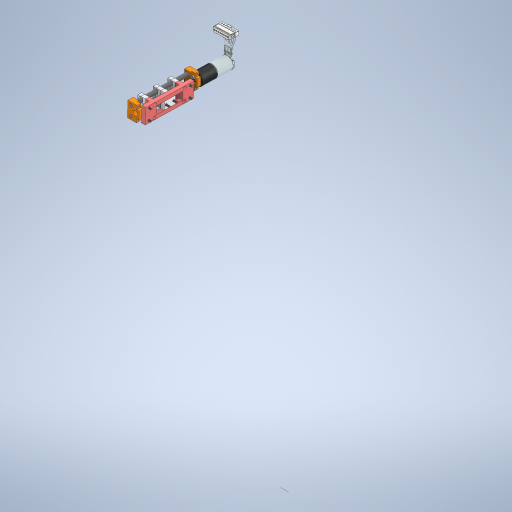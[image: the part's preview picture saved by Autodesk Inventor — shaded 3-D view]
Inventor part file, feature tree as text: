
AUTODESK INVENTOR PART (.ipt)
format: ipt  version: 2023 (Build 270158000, 158)  size: 17,346,048 bytes
history: native  units: mm
features: other x42, sketch x1
ambient origin geometry x8: Origin, YZ Plane, XZ Plane, XY Plane, X Axis, Y Axis, Z Axis, Center Point
bodies: Solid1 (feature_tree), Solid2 (feature_tree), Solid3 (feature_tree), Solid4 (feature_tree), Solid5 (feature_tree), Solid6 (feature_tree), Solid7 (feature_tree), Solid8 (feature_tree), Solid9 (feature_tree), Solid10 (feature_tree), Solid11 (feature_tree), Solid12 (feature_tree), Solid13 (feature_tree), Solid14 (feature_tree), Solid15 (feature_tree), Solid16 (feature_tree), Solid17 (feature_tree), Solid18 (feature_tree), Solid19 (feature_tree), Solid20 (feature_tree), Solid21 (feature_tree), Solid22 (feature_tree), Solid23 (feature_tree), Solid24 (feature_tree), Solid25 (feature_tree), Solid26 (feature_tree), Solid27 (feature_tree), Solid28 (feature_tree), Solid29 (feature_tree), Solid30 (feature_tree), Solid31 (feature_tree), Solid32 (feature_tree), Solid33 (feature_tree), Solid34 (feature_tree), Solid35 (feature_tree), Solid36 (feature_tree), Solid37 (feature_tree), Solid38 (feature_tree), Solid39 (feature_tree), Solid40 (feature_tree)
feature tree (43):
  other  "DifferentialLinearActuator.iam"
  other  "Part1.ipt:1"
  other  "GP16A_2-Stufig-110322.ipt:2"
  other  "283825_ec-max16_5w.ipt:2"
  other  "4145N198_Set Screw Precision Flexible Shaft Couplings.ipt:2"
  other  "91292A832_18-8 Stainless Steel Socket Head Screw.ipt:5"
  other  "91292A832_18-8 Stainless Steel Socket Head Screw.ipt:6"
  other  "MotorMountDifferential.ipt:1"
  other  "93805A627_18-8 Stainless Steel Threaded Rod.ipt:1"
  other  "93805A631_18-8 Stainless Steel Threaded Rod.ipt:2"
  other  "91828A113_18-8 Stainless Steel Hex Nut.ipt:1"
  other  "94450A564_Left-Hand Threaded 18-8 Stainless Steel Thin Hex Nut.ipt:3"
  other  "MotorDifferentialMountingBracket.ipt:1"
  other  "POMSliderMotorM25.ipt:1"
  other  "SliderFixtureM25.ipt:1"
  other  "POMSliderMotor.ipt:3"
  other  "POMSliderMotor.ipt:4"
  other  "91292A832_18-8 Stainless Steel Socket Head Screw.ipt:9"
  other  "91292A832_18-8 Stainless Steel Socket Head Screw.ipt:10"
  other  "91292A832_18-8 Stainless Steel Socket Head Screw.ipt:11"
  other  "91292A832_18-8 Stainless Steel Socket Head Screw.ipt:12"
  other  "91292A832_18-8 Stainless Steel Socket Head Screw.ipt:13"
  other  "91292A832_18-8 Stainless Steel Socket Head Screw.ipt:14"
  other  "91292A832_18-8 Stainless Steel Socket Head Screw.ipt:15"
  other  "91292A832_18-8 Stainless Steel Socket Head Screw.ipt:16"
  other  "91292A832_18-8 Stainless Steel Socket Head Screw.ipt:17"
  other  "91292A832_18-8 Stainless Steel Socket Head Screw.ipt:18"
  other  "AxisJoinerThreaded.ipt:2"
  other  "AxisLinear.ipt:1"
  other  "AxisLinear.ipt:2"
  other  "91292A832_18-8 Stainless Steel Socket Head Screw.ipt:19"
  other  "91292A832_18-8 Stainless Steel Socket Head Screw.ipt:20"
  other  "MotorMountDifferential.ipt:2"
  other  "91292A832_18-8 Stainless Steel Socket Head Screw.ipt:21"
  other  "91292A832_18-8 Stainless Steel Socket Head Screw.ipt:22"
  other  "POMSliderAxis.ipt:1"
  other  "POMSliderAxis.ipt:2"
  other  "POMSliderAxis.ipt:3"
  other  "91292A832_18-8 Stainless Steel Socket Head Screw.ipt:23"
  other  "91292A832_18-8 Stainless Steel Socket Head Screw.ipt:24"
  other  "91292A832_18-8 Stainless Steel Socket Head Screw.ipt:25"
  other  "Work Axis1"
  sketch  "Sketch6"  dims[d0=10.0mm]
